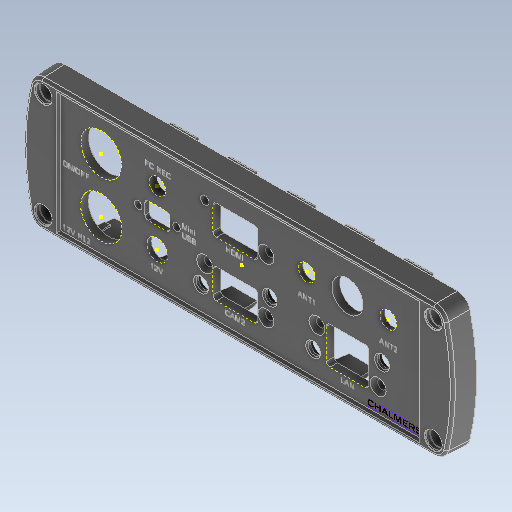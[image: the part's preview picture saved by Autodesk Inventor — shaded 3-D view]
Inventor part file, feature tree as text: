
AUTODESK INVENTOR PART (.ipt)
format: ipt  version: 2021 (Build 250183000, 183)  size: 1,268,736 bytes
history: native  units: mm
features: extrude x14, sketch x14, fillet x5, other x4, plane x3, chamfer x2, mirror x1, hole x1, reference x1
ambient origin geometry x8: Origin, YZ Plane, XZ Plane, XY Plane, X Axis, Y Axis, Z Axis, Center Point
bodies: Solid1 (feature_tree)
feature tree (45):
  other  "1009799_3D"
  extrude  "Extrusion1"  Depth=4.85mm
  fillet  "Fillet1"  Radius=27.0mm
  plane  "Work Plane1"
  extrude  "Extrusion2"  Depth=3.5mm
  chamfer  "Chamfer1"  [1 undecoded]
  plane  "Work Plane3"
  mirror  "Mirror2"
  extrude  "Extrusion7"  Depth=8.225mm
  extrude  "Extrusion8"  Depth=1.85mm
  extrude  "Extrusion9"  Depth=10.0mm TaperAngle=0.0deg
  extrude  "Extrusion10"  Depth=2.0mm
  extrude  "Extrusion11"  Depth=3.5mm
  fillet  "Fillet3"  Radius=3.725mm
  extrude  "Extrusion12"  Depth=3.5mm
  fillet  "Fillet4"  Radius=4.725mm
  extrude  "Extrusion13"  Depth=3.5mm
  extrude  "Extrusion14"  Depth=3.5mm
  hole  "Hole1"  [1 undecoded]
  extrude  "Extrusion16"  Depth=3.5mm
  fillet  "Fillet5"  Radius=7.0mm
  extrude  "Extrusion17"  Depth=7.0mm
  extrude  "Extrusion18"  Depth=7.0mm
  fillet  "Fillet6"  Radius=7.0mm
  extrude  "Extrusion19"  Depth=4.5mm
  chamfer  "Chamfer6"  Distance=4.5mm
  sketch  "Sketch29"  dims[d66=4.85mm d67=4.85mm d68=27.0mm d69=9.0mm d70=3.3mm d71=3.3mm d72=24.0mm d73=17.55mm d74=11.55mm d75=6.35mm d76=1.85mm d77=1.275mm d78=3.725mm d79=3.225mm d80=4.725mm d81=5.225mm d82=0.05mm d83=0.05mm d85=11.5mm d86=4.85mm d87=4.85mm d88=27.0mm d90=3.3mm d91=3.3mm d92=24.0mm d93=16.55mm d94=14.55mm d95=9.0mm d96=4.5mm d97=3.725mm d98=5.225mm d100=0.05mm d101=3.725mm d102=5.225mm d104=7.0mm d105=7.0mm d106=7.0mm d107=7.0mm d108=4.5mm d109=4.5mm d112=9.125mm d113=9.125mm d114=30.0mm d115=44.0mm d116=10.0mm d117=0.0mm d118=11.55mm d119=5.775mm d120=16.0mm d121=16.0mm d122=6.5mm d123=6.5mm d124=12.2mm d125=16.0mm d126=16.0mm d128=16.55mm d129=21.725mm d130=30.0mm d132=10.075mm d134=16.2mm d135=8.13mm d136=0.0mm d137=22.0mm d138=0.0mm d139=0.0mm d141=6.35mm d142=0.0mm d143=0.0mm d144=10.0mm d145=0.0mm d147=1.275mm d148=1.275mm d149=13.908852mm d150=0.7125mm d151=11.55mm d152=5.775mm d154=11.55mm d155=9.75mm d156=6.75mm d157=3.0mm d158=7.5mm d159=0.0mm d160=0.0mm d161=1.25mm d164=16.0mm d165=4.875mm d166=9.75mm d167=22.0mm d168=11.0mm d169=1.5mm d170=0.0mm d171=2.0mm d172=12.4mm d173=0.0mm d174=0.0mm d175=1.5mm d176=0.0mm d177=6.5mm d178=0.0mm d179=0.0mm d199=3.25mm d200=6.0mm d201=6.25mm d202=2.0mm d203=90.0deg d204=8.0mm d205=20.594885mm d206=13.0mm d207=10.0mm d208=0.0mm d209=2.0mm d210=14.0mm d211=14.0mm d212=1.5mm d213=0.0mm d214=20.0mm d215=0.2mm d216=0.0mm d217=0.0mm d218=3.0mm d219=20.0mm d220=0.0mm d221=7.877954mm d222=0.2mm d223=2.0mm d224=45.0deg d225=1.5mm d226=0.8mm d227=0.8mm d228=1.5mm d229=0.85mm d230=6.75mm d231=4.75mm d232=5.0mm d233=2.75mm d234=3.5mm d235=1.5mm d236=5.0mm d237=1.0mm d238=1.0mm d239=4.75mm d240=1.0mm d241=5.5mm d242=4.5mm d243=4.5mm d244=3.5mm d245=3.5mm]
  plane  "Work Plane2"
  sketch  "Sketch10"  dims[d0=4.85mm d1=4.85mm d2=27.0mm]
  sketch  "Sketch11"  dims[d3=9.0mm d4=3.5mm]
  sketch  "Sketch12"  dims[d6=3.3mm]
  sketch  "Sketch13"  dims[d7=3.3mm]
  sketch  "Sketch14"  dims[d8=24.0mm]
  sketch  "Sketch15"  dims[d9=5.0mm]
  sketch  "Sketch16"  dims[d11=16.55mm]
  sketch  "Sketch17"  dims[d12=11.55mm]
  reference  "Reference1"
  sketch  "Sketch23"  dims[d14=17.0mm d15=0.0mm d16=0.0mm]
  sketch  "Sketch24"  dims[d17=6.35mm d20=8.225mm]
  sketch  "Sketch25"  dims[d21=6.9mm d22=1.85mm]
  sketch  "Sketch26"  dims[d23=1.35mm d26=-1.5mm d27=10.0mm d28=0.0mm]
  sketch  "Sketch27"  dims[d29=0.5mm d30=2.0mm d31=45.0deg d65=9.408852mm]
  other  "Image1"
  other  "<userpath>\Google Drive\Unicorn 2020\CAD\Assembly.iam"
  other  "Assembly.iam"
note: 2 required parameter values undecoded (feature->parameter linkage not recoverable at this tier; creation-order binding heuristic only, values carry confidence <= 0.55)
